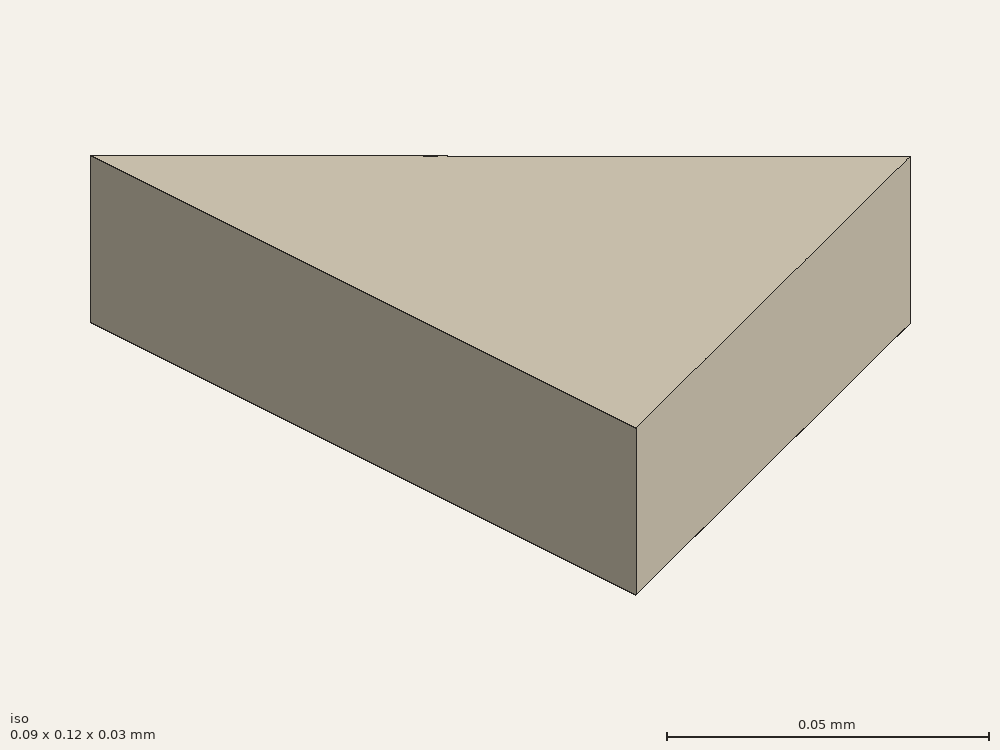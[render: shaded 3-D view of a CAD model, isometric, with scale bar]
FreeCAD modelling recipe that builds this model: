
FCSTD DOCUMENT  (FreeCAD 0.15R4671 (Git))
Label: triangle4
License: All rights reserved
LicenseURL: http://en.wikipedia.org/wiki/All_rights_reserved
objects: Sketcher::SketchObject×1, PartDesign::Pad×1
note: 3 computed .brp shape members not serialized (recipe doc carries the construction recipe); baked Part::Feature solids carry a one-line shape summary decoded from their .brp

FEATURE [Sketcher::SketchObject] Sketch
  sketch-geometry (3):
    g0: LineSegment StartX=-0.03 StartY=0.0701395 StartZ=0 EndX=-0.03 EndY=-0.0498605 EndZ=0
    g1: LineSegment StartX=-0.03 StartY=-0.0498605 StartZ=0 EndX=0.06 EndY=-0.020279 EndZ=0
    g2: LineSegment StartX=0.06 StartY=-0.020279 StartZ=0 EndX=-0.03 EndY=0.0701395 EndZ=0
  constraints (9):
    c: Coincident(g0,g1)
    c: Coincident(g1,g2)
    c: Coincident(g0,g2)
    c: Distance(g1,g0) = 0.09
    c: Distance(g-1,g0) = 0.03
    c: Distance(g0) = 0.12
    c: Parallel(g0,g-2)
    c: Distance(g0,g1) = 0.114
    c: Distance(g-1,g1) = 0.038
FEATURE [PartDesign::Pad] Pad
  Length = 0.03
  Length2 = 100
  Midplane = true
  Sketch = -> Sketch
  Type = 0
